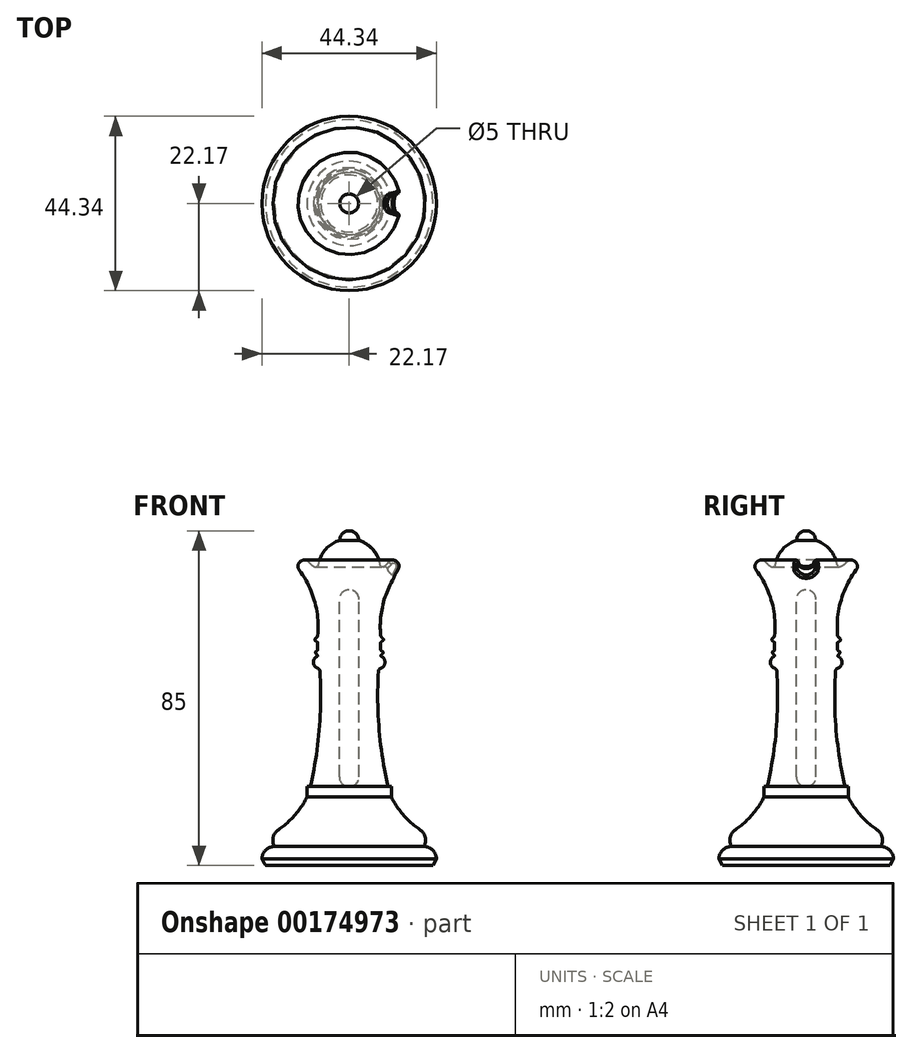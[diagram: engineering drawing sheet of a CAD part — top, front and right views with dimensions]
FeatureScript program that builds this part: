
annotation { "Feature Type Name" : "Feature", "Feature Type Description" : "" }
export const myFeature = defineFeature(function(context is Context, id is Id, definition is map)
    precondition{}
    {
        {
            var Q0;
            Q0=qCreatedBy(makeId("Front.planeOp"),FACE);
            var sketch = newSketch(context, id + "F0", { "sketchPlane" : qUnion([Q0])});
            skLineSegment(sketch, "E0", {"start": v(0, 0) * mm, "end": v(21.25, 0) * mm});
            skLineSegment(sketch, "E1", {"start": v(0, 0) * mm, "end": v(0, 95) * mm, "construction": true});
            skLineSegment(sketch, "E2", {"start": v(0, 20) * mm, "end": v(10.7, 20) * mm, "construction": true});
            skLineSegment(sketch, "E3", {"start": v(14.4, 50) * mm, "end": v(0, 50) * mm, "construction": true});
            skLineSegment(sketch, "E4", {"start": v(0, 75) * mm, "end": v(12.7, 75) * mm, "construction": true});
            skLineSegment(sketch, "E5", {"start": v(0, 64.34) * mm, "end": v(14.8, 64.34) * mm, "construction": true});
            skLineSegment(sketch, "E6", {"start": v(21.25, 0) * mm, "end": v(22.17, 1.6) * mm});
            skArc(sketch, "E7", {"start": v(22.17, 1.6) * mm, "mid": v(21.24, 3.86) * mm, "end": v(18.97, 4.8) * mm});
            skLineSegment(sketch, "E8", {"start": v(10.7, 20) * mm, "end": v(10.7, 17.37) * mm});
            skArc(sketch, "E9", {"start": v(10.7, 17.37) * mm, "mid": v(13.82, 12.74) * mm, "end": v(18, 9.05) * mm});
            skArc(sketch, "E10", {"start": v(18.97, 4.8) * mm, "mid": v(19.32, 7.12) * mm, "end": v(18, 9.05) * mm});
            skLineSegment(sketch, "E11", {"start": v(10.7, 20) * mm, "end": v(9.9, 20) * mm});
            skArc(sketch, "E12", {"start": v(7.5, 50) * mm, "mid": v(7.56, 34.9) * mm, "end": v(9.9, 20) * mm});
            skArc(sketch, "E13", {"start": v(7.5, 50) * mm, "mid": v(9.09, 51.4) * mm, "end": v(7.9, 53.15) * mm});
            skLineSegment(sketch, "E14", {"start": v(7.9, 53.15) * mm, "end": v(8.7, 54.1) * mm});
            skLineSegment(sketch, "E15", {"start": v(8.7, 54.1) * mm, "end": v(8, 54.69) * mm});
            skLineSegment(sketch, "E16", {"start": v(8, 54.69) * mm, "end": v(8, 56.63) * mm});
            skLineSegment(sketch, "E17", {"start": v(8, 56.63) * mm, "end": v(8.8, 57.3) * mm});
            skLineSegment(sketch, "E18", {"start": v(8.8, 57.3) * mm, "end": v(8, 58.26) * mm});
            skLineSegment(sketch, "E19", {"start": v(3.2, 78.2) * mm, "end": v(0, 78.2) * mm});
            skLineSegment(sketch, "E20", {"start": v(0, 78.2) * mm, "end": v(0, 0) * mm});
            skArc(sketch, "E21", {"start": v(12.7, 75) * mm, "mid": v(8.78, 67.07) * mm, "end": v(8, 58.26) * mm});
            skArc(sketch, "E22", {"start": v(12.7, 75) * mm, "mid": v(12.4, 77.23) * mm, "end": v(10.16, 76.95) * mm});
            skArc(sketch, "E23", {"start": v(3.2, 78.2) * mm, "mid": v(6.3, 75.48) * mm, "end": v(10.16, 76.95) * mm});
            skSolve(sketch);
        }
        {
            var Q0;
            Q0=qSketchRegion(id+"F0",true);
            var Q1;
            Q1=sQuery(id+"F0.wireOp",EDGE,"E1");
            revolve(context, id + "F1", {"entities" : qUnion([Q0]), "axis" : qUnion([Q1]), "revolveType" : RevolveType.FULL});
        }
        {
            var Q0;
            Q0=makeQuery(id+"F1.opRevolve","SWEPT_EDGE",EDGE,{"disambiguationData":[OSD([sQuery(id+"F0.wireOp",EDGE,"E12"),sQuery(id+"F0.wireOp",EDGE,"E13")])]});
            var Q1;
            Q1=makeQuery(id+"F1.opRevolve","SWEPT_EDGE",EDGE,{"disambiguationData":[OSD([sQuery(id+"F0.wireOp",EDGE,"E11"),sQuery(id+"F0.wireOp",EDGE,"E12")])]});
            fillet(context, id + "F2", {"entities" : qUnion([Q0, Q1]), "radius" : .8 * mm, "tangentPropagation" : true, "allowEdgeOverflow" : false});
        }
        {
            var Q0;
            Q0=makeQuery(id+"F1.opRevolve","SWEPT_EDGE",EDGE,{"disambiguationData":[OSD([sQuery(id+"F0.wireOp",EDGE,"E17"),sQuery(id+"F0.wireOp",EDGE,"E18")])]});
            var Q1;
            Q1=makeQuery(id+"F1.opRevolve","SWEPT_EDGE",EDGE,{"disambiguationData":[OSD([sQuery(id+"F0.wireOp",EDGE,"E14"),sQuery(id+"F0.wireOp",EDGE,"E15")])]});
            var Q2;
            Q2=makeQuery(id+"F1.opRevolve","SWEPT_EDGE",EDGE,{"disambiguationData":[OSD([sQuery(id+"F0.wireOp",EDGE,"OAx1KunF-KjKq-zgV9-Glhn-Sdbq04AqaJ7j"),sQuery(id+"F0.wireOp",EDGE,"E18")])]});
            var Q3;
            Q3=makeQuery(id+"F1.opRevolve","SWEPT_EDGE",EDGE,{"disambiguationData":[OSD([sQuery(id+"F0.wireOp",EDGE,"E16"),sQuery(id+"F0.wireOp",EDGE,"E17")])]});
            var Q4;
            Q4=makeQuery(id+"F1.opRevolve","SWEPT_EDGE",EDGE,{"disambiguationData":[OSD([sQuery(id+"F0.wireOp",EDGE,"E15"),sQuery(id+"F0.wireOp",EDGE,"E16")])]});
            var Q5;
            Q5=makeQuery(id+"F1.opRevolve","SWEPT_EDGE",EDGE,{"disambiguationData":[OSD([sQuery(id+"F0.wireOp",EDGE,"E13"),sQuery(id+"F0.wireOp",EDGE,"E14")])]});
            fillet(context, id + "F3", {"entities" : qUnion([Q0, Q1, Q2, Q3, Q4, Q5]), "radius" : .2 * mm, "tangentPropagation" : true, "allowEdgeOverflow" : false});
        }
        {
            var Q0;
            Q0=qCreatedBy(makeId("Front.planeOp"),FACE);
            var sketch = newSketch(context, id + "F4", { "sketchPlane" : qUnion([Q0])});
            skLineSegment(sketch, "E24.bottom", {"start": v(0, 20) * mm, "end": v(0, 20) * mm});
            skLineSegment(sketch, "E24.top", {"start": v(0, 70) * mm, "end": v(0, 70) * mm});
            skLineSegment(sketch, "E24.left", {"start": v(2.5, 22.5) * mm, "end": v(2.5, 67.5) * mm});
            skPoint(sketch, "E24.middle", {"position": v(0, 45) * mm});
            skPoint(sketch, "E25.visualSharp", {"position": v(2.5, 70) * mm});
            skArc(sketch, "E25.filletArc", {"start": v(2.5, 67.5) * mm, "mid": v(1.77, 69.27) * mm, "end": v(0, 70) * mm});
            skPoint(sketch, "E26.visualSharp", {"position": v(-2.5, 70) * mm});
            skPoint(sketch, "E27.visualSharp", {"position": v(-2.5, 20) * mm});
            skPoint(sketch, "E28.visualSharp", {"position": v(2.5, 20) * mm});
            skArc(sketch, "E28.filletArc", {"start": v(0, 20) * mm, "mid": v(1.77, 20.73) * mm, "end": v(2.5, 22.5) * mm});
            skLineSegment(sketch, "E29", {"start": v(0, 70) * mm, "end": v(0, 20) * mm});
            skSolve(sketch);
        }
        {
            var Q0;
            Q0=qSketchRegion(id+"F4",true);
            var Q1;
            Q1=qConstructionFilter(qBodyType(qCreatedBy(id+"F4",EDGE),BodyType.WIRE),ConstructionObject.NO);
            var Q2;
            Q2=sQuery(id+"F4.wireOp",EDGE,"E29");
            revolve(context, id + "F5", {"operationType" : NewBodyOperationType.REMOVE, "entities" : qUnion([Q0]), "surfaceEntities" : qUnion([Q1]), "axis" : qUnion([Q2]), "revolveType" : RevolveType.FULL});
        }
        {
            var Q0;
            Q0=qCreatedBy(makeId("Front.planeOp"),FACE);
            var sketch = newSketch(context, id + "F6", { "sketchPlane" : qUnion([Q0])});
            skLineSegment(sketch, "E30", {"start": v(0, 85) * mm, "end": v(0, 72.2) * mm});
            skArc(sketch, "E31", {"start": v(0, 85) * mm, "mid": v(1.7, 84.3) * mm, "end": v(2.4, 82.6) * mm});
            skArc(sketch, "E32", {"start": v(2.4, 82.6) * mm, "mid": v(6.45, 79.7) * mm, "end": v(8, 74.97) * mm});
            skLineSegment(sketch, "E33", {"start": v(0, 74.97) * mm, "end": v(8, 74.97) * mm});
            skSolve(sketch);
        }
        {
            var Q0;
            Q0 = qSketchRegion(id + "F6", true);
            var Q1;
            Q1=sQuery(id+"F6.wireOp",EDGE,"E30");
            revolve(context, id + "F7", {"operationType" : NewBodyOperationType.ADD, "entities" : qUnion([Q0]), "axis" : qUnion([Q1]), "revolveType" : RevolveType.FULL});
        }
        {
            var Q0;
            Q0=qCreatedBy(makeId("Front.planeOp"),FACE);
            var sketch = newSketch(context, id + "F8", { "sketchPlane" : qUnion([Q0])});
            skLineSegment(sketch, "E34", {"start": v(12, 73.6) * mm, "end": v(12, 78.4) * mm});
            skArc(sketch, "E35", {"start": v(12, 78.4) * mm, "mid": v(14.4, 76) * mm, "end": v(12, 73.6) * mm});
            skSolve(sketch);
        }
        {
            var Q0;
            Q0 = qSketchRegion(id + "F8", true);
            var Q1;
            Q1=sQuery(id+"F8.wireOp",EDGE,"E34");
            revolve(context, id + "F9", {"operationType" : NewBodyOperationType.REMOVE, "entities" : qUnion([Q0]), "axis" : qUnion([Q1]), "revolveType" : RevolveType.FULL, "oppositeDirection" : true});
        }
        {
            var Q0;
            Q0=makeQuery(id+"FEuoNlddHJfP73j_1.4.F9.boolean.opBoolean","COPY",FACE,{"derivedFrom":makeQuery(id+"FEuoNlddHJfP73j_1.4.F9.opRevolve","SWEPT_FACE",FACE,{"disambiguationData":[OSD([sQuery(id+"F8.wireOp",EDGE,"E35")])]})});
            var Q1;
            Q1=makeQuery(id+"FEuoNlddHJfP73j_1.5.F9.boolean.opBoolean","COPY",FACE,{"derivedFrom":makeQuery(id+"FEuoNlddHJfP73j_1.5.F9.opRevolve","SWEPT_FACE",FACE,{"disambiguationData":[OSD([sQuery(id+"F8.wireOp",EDGE,"E35")])]})});
            var Q2;
            Q2=makeQuery(id+"FEuoNlddHJfP73j_1.3.F9.boolean.opBoolean","COPY",FACE,{"derivedFrom":makeQuery(id+"FEuoNlddHJfP73j_1.3.F9.opRevolve","SWEPT_FACE",FACE,{"disambiguationData":[OSD([sQuery(id+"F8.wireOp",EDGE,"E35")])]})});
            var Q3;
            Q3=makeQuery(id+"FEuoNlddHJfP73j_1.2.F9.boolean.opBoolean","COPY",FACE,{"derivedFrom":makeQuery(id+"FEuoNlddHJfP73j_1.2.F9.opRevolve","SWEPT_FACE",FACE,{"disambiguationData":[OSD([sQuery(id+"F8.wireOp",EDGE,"E35")])]})});
            var Q4;
            Q4=makeQuery(id+"FEuoNlddHJfP73j_1.1.F9.boolean.opBoolean","COPY",FACE,{"derivedFrom":makeQuery(id+"FEuoNlddHJfP73j_1.1.F9.opRevolve","SWEPT_FACE",FACE,{"disambiguationData":[OSD([sQuery(id+"F8.wireOp",EDGE,"E35")])]})});
            var Q5;
            Q5=makeQuery(id+"F9.boolean.opBoolean","COPY",FACE,{"derivedFrom":makeQuery(id+"F9.opRevolve","SWEPT_FACE",FACE,{"disambiguationData":[OSD([sQuery(id+"F8.wireOp",EDGE,"E35")])]})});
            var Q6;
            Q6=makeQuery(id+"FEuoNlddHJfP73j_1.6.F9.boolean.opBoolean","COPY",FACE,{"derivedFrom":makeQuery(id+"FEuoNlddHJfP73j_1.6.F9.opRevolve","SWEPT_FACE",FACE,{"disambiguationData":[OSD([sQuery(id+"F8.wireOp",EDGE,"E35")])]})});
            var Q7;
            Q7=makeQuery(id+"FEuoNlddHJfP73j_1.7.F9.boolean.opBoolean","COPY",FACE,{"derivedFrom":makeQuery(id+"FEuoNlddHJfP73j_1.7.F9.opRevolve","SWEPT_FACE",FACE,{"disambiguationData":[OSD([sQuery(id+"F8.wireOp",EDGE,"E35")])]})});
            var Q8;
            Q8=makeQuery(id+"FEuoNlddHJfP73j_1.8.F9.boolean.opBoolean","COPY",FACE,{"derivedFrom":makeQuery(id+"FEuoNlddHJfP73j_1.8.F9.opRevolve","SWEPT_FACE",FACE,{"disambiguationData":[OSD([sQuery(id+"F8.wireOp",EDGE,"E35")])]})});
            var Q9;
            Q9=makeQuery(id+"FEuoNlddHJfP73j_1.9.F9.boolean.opBoolean","COPY",FACE,{"derivedFrom":makeQuery(id+"FEuoNlddHJfP73j_1.9.F9.opRevolve","SWEPT_FACE",FACE,{"disambiguationData":[OSD([sQuery(id+"F8.wireOp",EDGE,"E35")])]})});
            var Q10;
            Q10=makeQuery(id+"F7.boolean.opBoolean","INTERSECT",EDGE,{"derivedFrom":[makeQuery(id+"F1.opRevolve","SWEPT_FACE",FACE,{"disambiguationData":[OSD([sQuery(id+"F0.wireOp",EDGE,"E23")])]}),makeQuery(id+"F7.opRevolve","SWEPT_FACE",FACE,{"disambiguationData":[OSD([sQuery(id+"F6.wireOp",EDGE,"E32")])]})]});
            fillet(context, id + "F10", {"entities" : qUnion([Q0, Q1, Q2, Q3, Q4, Q5, Q6, Q7, Q8, Q9, Q10]), "radius" : .6 * mm, "tangentPropagation" : true, "allowEdgeOverflow" : false});
        }
    });
